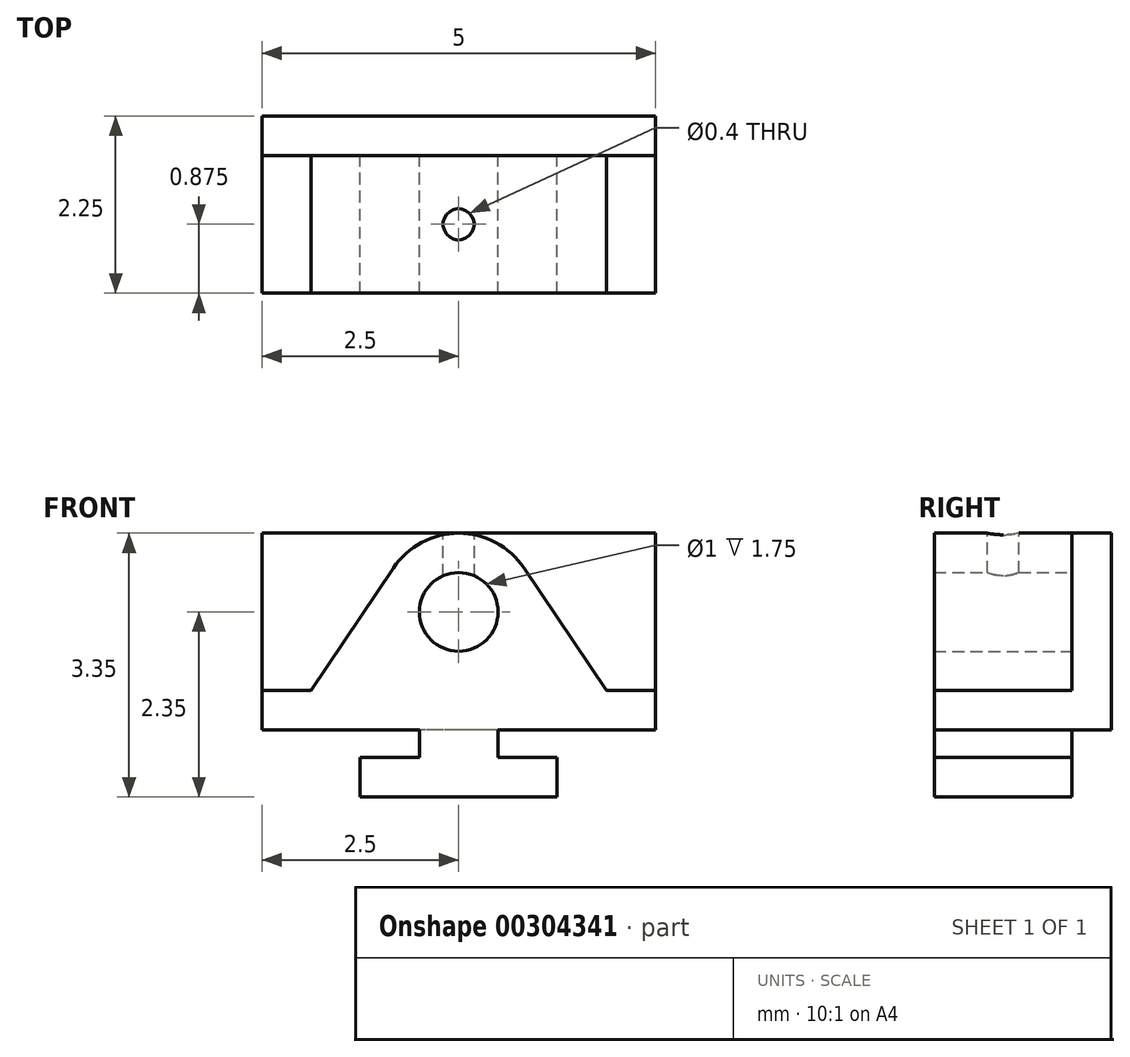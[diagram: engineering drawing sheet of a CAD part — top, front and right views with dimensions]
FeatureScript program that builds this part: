
annotation { "Feature Type Name" : "Feature", "Feature Type Description" : "" }
export const myFeature = defineFeature(function(context is Context, id is Id, definition is map)
    precondition{}
    {
        {
            var Q0;
            Q0=qCreatedBy(makeId("Front.planeOp"),FACE);
            var sketch = newSketch(context, id + "F0", { "sketchPlane" : qUnion([Q0])});
            skCircle(sketch, "E0", {"center": v(0, 0) * mm, "radius": 0.5 * mm});
            skLineSegment(sketch, "E1", {"start": v(-2.5, -1.5) * mm, "end": v(-0.5, -1.5) * mm});
            skLineSegment(sketch, "E2", {"start": v(-0.5, -1.5) * mm, "end": v(-0.5, -1.85) * mm});
            skLineSegment(sketch, "E3", {"start": v(-0.5, -1.85) * mm, "end": v(-1.25, -1.85) * mm});
            skLineSegment(sketch, "E4", {"start": v(-1.25, -1.85) * mm, "end": v(-1.25, -2.35) * mm});
            skLineSegment(sketch, "E5", {"start": v(-1.25, -2.35) * mm, "end": v(0, -2.35) * mm});
            skLineSegment(sketch, "E6", {"start": v(-2.5, -1.5) * mm, "end": v(-2.5, -1) * mm});
            skLineSegment(sketch, "E7", {"start": v(-2.5, -1) * mm, "end": v(-1.88, -1) * mm});
            skLineSegment(sketch, "E8", {"start": v(-1.88, -1) * mm, "end": v(-0.83, 0.56) * mm});
            skLineSegment(sketch, "E9.MirrorCS", {"start": v(1.25, -2.35) * mm, "end": v(0, -2.35) * mm});
            skLineSegment(sketch, "E10.MirrorCS", {"start": v(1.25, -1.85) * mm, "end": v(1.25, -2.35) * mm});
            skLineSegment(sketch, "E11.MirrorCS", {"start": v(0.5, -1.5) * mm, "end": v(0.5, -1.85) * mm});
            skLineSegment(sketch, "E12.MirrorCS", {"start": v(0.5, -1.85) * mm, "end": v(1.25, -1.85) * mm});
            skLineSegment(sketch, "E13.MirrorCS", {"start": v(1.88, -1) * mm, "end": v(0.83, 0.56) * mm});
            skLineSegment(sketch, "E14.MirrorCS", {"start": v(2.5, -1) * mm, "end": v(1.88, -1) * mm});
            skLineSegment(sketch, "E15.MirrorCS", {"start": v(2.5, -1.5) * mm, "end": v(0.5, -1.5) * mm});
            skLineSegment(sketch, "E16.MirrorCS", {"start": v(2.5, -1.5) * mm, "end": v(2.5, -1) * mm});
            skArc(sketch, "E17", {"start": v(-0.83, 0.56) * mm, "mid": v(0, 1) * mm, "end": v(0.83, 0.56) * mm});
            skSolve(sketch);
        }
        {
            var Q0;
            Q0 = qSketchRegion(id + "F0", true);
            extrude(context, id + "F1", {"entities" : qUnion([Q0]), "depth" : (2.25 - .5) * mm});
        }
        {
            var Q0;
            Q0=makeQuery(id+"F1.opExtrude","CAP_FACE",FACE,{"disambiguationData":[OSD([sQuery(id+"F0.wireOp",EDGE,"E0"),sQuery(id+"F0.wireOp",EDGE,"E1"),sQuery(id+"F0.wireOp",EDGE,"E2"),sQuery(id+"F0.wireOp",EDGE,"E3"),sQuery(id+"F0.wireOp",EDGE,"E4"),sQuery(id+"F0.wireOp",EDGE,"E5"),sQuery(id+"F0.wireOp",EDGE,"E6"),sQuery(id+"F0.wireOp",EDGE,"E7"),sQuery(id+"F0.wireOp",EDGE,"E8"),sQuery(id+"F0.wireOp",EDGE,"E9.MirrorCS"),sQuery(id+"F0.wireOp",EDGE,"E10.MirrorCS"),sQuery(id+"F0.wireOp",EDGE,"E11.MirrorCS"),sQuery(id+"F0.wireOp",EDGE,"E12.MirrorCS"),sQuery(id+"F0.wireOp",EDGE,"E13.MirrorCS"),sQuery(id+"F0.wireOp",EDGE,"E14.MirrorCS"),sQuery(id+"F0.wireOp",EDGE,"E15.MirrorCS"),sQuery(id+"F0.wireOp",EDGE,"E16.MirrorCS"),sQuery(id+"F0.wireOp",EDGE,"E17")])],"isStart":true});
            var sketch = newSketch(context, id + "F2", { "sketchPlane" : qUnion([Q0])});
            skLineSegment(sketch, "E18.bottom", {"start": v(-2.5, -1.5) * mm, "end": v(2.5, -1.5) * mm});
            skLineSegment(sketch, "E18.top", {"start": v(-2.5, 1) * mm, "end": v(2.5, 1) * mm});
            skLineSegment(sketch, "E18.left", {"start": v(-2.5, -1.5) * mm, "end": v(-2.5, 1) * mm});
            skLineSegment(sketch, "E18.right", {"start": v(2.5, -1.5) * mm, "end": v(2.5, 1) * mm});
            skSolve(sketch);
        }
        {
            var Q0;
            Q0 = qSketchRegion(id + "F2", true);
            extrude(context, id + "F3", {"entities" : qUnion([Q0]), "operationType" : NewBodyOperationType.ADD, "depth" : .5 * mm});
        }
        {
            var Q0;
            Q0=makeQuery(id+"F1.opExtrude","SWEPT_FACE",FACE,{"disambiguationData":[OSD([sQuery(id+"F0.wireOp",EDGE,"E5"),sQuery(id+"F0.wireOp",EDGE,"E9.MirrorCS")])]});
            cPlane(context, id + "F4", {"entities" : qUnion([Q0]), "cplaneType" : CPlaneType.OFFSET, "offset" : 3.35 * mm, "oppositeDirection" : true, "width" : 150 * mm, "height" : 150 * mm});
        }
        {
            var Q0;
            Q0=qCreatedBy(id+"F4.planeOp",FACE);
            var sketch = newSketch(context, id + "F5", { "sketchPlane" : qUnion([Q0])});
            skCircle(sketch, "E19", {"center": v(0, 0.87) * mm, "radius": 0.2 * mm});
            skSolve(sketch);
        }
        {
            var Q0;
            Q0 = qSketchRegion(id + "F5", true);
            extrude(context, id + "F6", {"entities" : qUnion([Q0]), "operationType" : NewBodyOperationType.REMOVE, "endBound" : BoundingType.UP_TO_NEXT, "depth" : 25 * mm});
        }
    });
